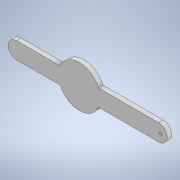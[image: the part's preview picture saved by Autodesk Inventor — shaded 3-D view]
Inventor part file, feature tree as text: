
AUTODESK INVENTOR PART (.ipt)
format: ipt  version: 2022 (Build 260153000, 153)  size: 136,192 bytes
history: native  units: mm
features: extrude x3, sketch x3, other x1
ambient origin geometry x8: Origin, YZ Plane, XZ Plane, XY Plane, X Axis, Y Axis, Z Axis, Center Point
bodies: Body1 (feature_tree)
feature tree (7):
  other  "Sólido1"
  extrude  "Extrusión1"  Depth=20.0mm
  extrude  "Extrusión2"  Depth=20.0mm
  extrude  "Extrusión3"  Depth=25.0mm
  sketch  "Boceto1"  dims[d4=20.0mm d6=130.0mm]
  sketch  "Boceto2"  dims[d7=20.0mm d8=50.0mm]
  sketch  "Boceto4"  dims[d9=5.5mm d10=0.0mm d11=25.0mm d12=20.0mm d13=3.0mm d14=30.0mm d15=5.5mm d16=0.0mm d17=30.0mm d18=20.0mm d19=5.5mm d20=0.0mm]
